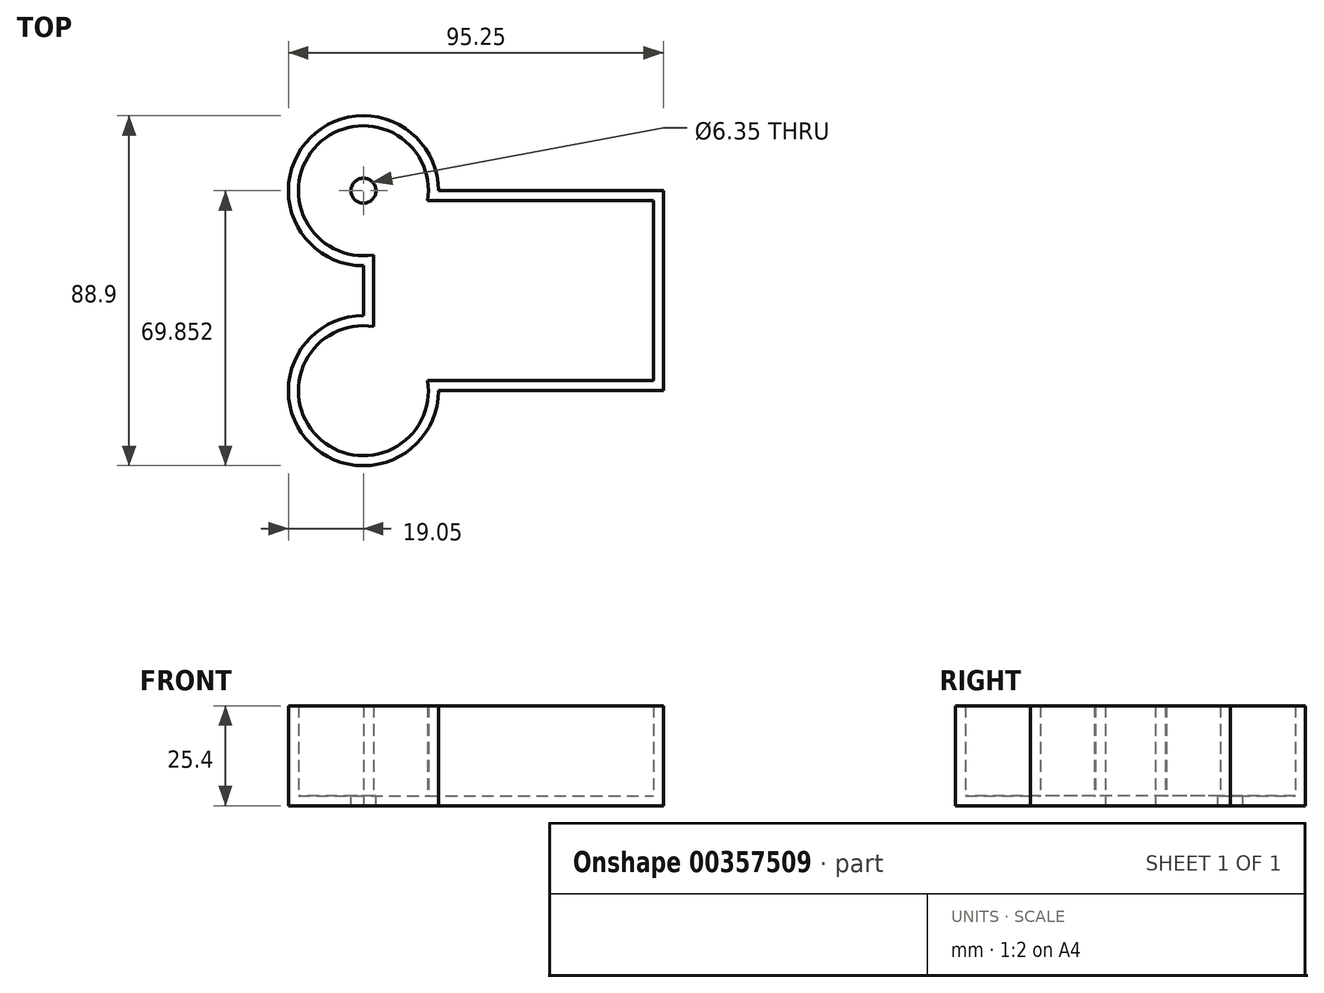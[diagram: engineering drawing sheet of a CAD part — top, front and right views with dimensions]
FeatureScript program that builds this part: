
annotation { "Feature Type Name" : "Feature", "Feature Type Description" : "" }
export const myFeature = defineFeature(function(context is Context, id is Id, definition is map)
    precondition{}
    {
        {
            var Q0;
            Q0=qCreatedBy(makeId("Top.planeOp"),FACE);
            var sketch = newSketch(context, id + "F0", { "sketchPlane" : qUnion([Q0])});
            skLineSegment(sketch, "E0.bottom", {"start": v(-34.16, 28.81) * mm, "end": v(42.04, 28.81) * mm});
            skLineSegment(sketch, "E0.top", {"start": v(-34.16, -21.99) * mm, "end": v(42.04, -21.99) * mm});
            skLineSegment(sketch, "E0.left", {"start": v(-34.16, 28.81) * mm, "end": v(-34.16, -21.99) * mm});
            skLineSegment(sketch, "E0.right", {"start": v(42.04, 28.81) * mm, "end": v(42.04, -21.99) * mm});
            skCircle(sketch, "E1", {"center": v(-34.16, 28.81) * mm, "radius": 19.05 * mm});
            skCircle(sketch, "E2", {"center": v(-34.16, -21.99) * mm, "radius": 19.05 * mm});
            skSolve(sketch);
        }
        {
            var Q0;
            {var subQ0=sQuery(id+"F0.wireOp",EDGE,"E0.right");Q0=makeQuery(id+"F0.imprint","IMPRINT",FACE,{"disambiguationData":[TD([[makeQuery(id+"F0.imprint","IMPRINT",EDGE,{"derivedFrom":subQ0}),-1.0]])]});}
            var Q1;
            {var subQ0=sQuery(id+"F0.wireOp",EDGE,"E0.left");var subQ1=sQuery(id+"F0.wireOp",EDGE,"E0.top");var subQ2=makeQuery(id+"F0.imprint","INTERSECT",VERTEX,{"derivedFrom":[subQ1,subQ0]});Q1=makeQuery(id+"F0.imprint","IMPRINT",FACE,{"disambiguationData":[TD([[makeQuery(id+"F0.imprint","IMPRINT",EDGE,{"disambiguationData":[TD([[subQ2,-1.0]])],"derivedFrom":subQ1}),1.0]])]});}
            var Q2;
            {var subQ0=sQuery(id+"F0.wireOp",EDGE,"E0.left");var subQ1=sQuery(id+"F0.wireOp",EDGE,"E0.top");var subQ2=makeQuery(id+"F0.imprint","INTERSECT",VERTEX,{"derivedFrom":[subQ1,subQ0]});Q2=makeQuery(id+"F0.imprint","IMPRINT",FACE,{"disambiguationData":[TD([[makeQuery(id+"F0.imprint","IMPRINT",EDGE,{"disambiguationData":[TD([[subQ2,-1.0]])],"derivedFrom":subQ1}),-1.0]])]});}
            var Q3;
            {var subQ0=sQuery(id+"F0.wireOp",EDGE,"E0.left");var subQ1=sQuery(id+"F0.wireOp",EDGE,"E0.bottom");var subQ2=makeQuery(id+"F0.imprint","INTERSECT",VERTEX,{"derivedFrom":[subQ1,subQ0]});Q3=makeQuery(id+"F0.imprint","IMPRINT",FACE,{"disambiguationData":[TD([[makeQuery(id+"F0.imprint","IMPRINT",EDGE,{"disambiguationData":[TD([[subQ2,-1.0]])],"derivedFrom":subQ1}),1.0]])]});}
            var Q4;
            {var subQ0=sQuery(id+"F0.wireOp",EDGE,"E0.left");var subQ1=sQuery(id+"F0.wireOp",EDGE,"E0.bottom");var subQ2=makeQuery(id+"F0.imprint","INTERSECT",VERTEX,{"derivedFrom":[subQ1,subQ0]});Q4=makeQuery(id+"F0.imprint","IMPRINT",FACE,{"disambiguationData":[TD([[makeQuery(id+"F0.imprint","IMPRINT",EDGE,{"disambiguationData":[TD([[subQ2,-1.0]])],"derivedFrom":subQ1}),-1.0]])]});}
            extrude(context, id + "F1", {"entities" : qUnion([Q0, Q1, Q2, Q3, Q4]), "depth" : 25.4 * mm});
        }
        {
            var Q0;
            Q0=makeQuery(id+"F1.opExtrude","CAP_FACE",FACE,{"disambiguationData":[OSD([sQuery(id+"F0.wireOp",EDGE,"E0.bottom"),sQuery(id+"F0.wireOp",EDGE,"E0.top"),sQuery(id+"F0.wireOp",EDGE,"E0.left"),sQuery(id+"F0.wireOp",EDGE,"E0.right"),sQuery(id+"F0.wireOp",EDGE,"E1"),sQuery(id+"F0.wireOp",EDGE,"E2")])],"isStart":false});
            shell(context, id + "F2", {"entities" : qUnion([Q0]), "thickness" : 2.54 * mm});
        }
        {
            var Q0;
            Q0=makeQuery(id+"F2.opShell","OFFSET_FACE",FACE,{"disambiguationData":[OSD([sQuery(id+"F0.wireOp",EDGE,"E0.bottom"),sQuery(id+"F0.wireOp",EDGE,"E0.top"),sQuery(id+"F0.wireOp",EDGE,"E0.left"),sQuery(id+"F0.wireOp",EDGE,"E0.right"),sQuery(id+"F0.wireOp",EDGE,"E1"),sQuery(id+"F0.wireOp",EDGE,"E2")])]});
            var sketch = newSketch(context, id + "F3", { "sketchPlane" : qUnion([Q0])});
            skCircle(sketch, "E3", {"center": v(-34.16, 28.81) * mm, "radius": 6.64 * mm});
            skCircle(sketch, "E4", {"center": v(-34.16, -21.99) * mm, "radius": 7.46 * mm});
            skSolve(sketch);
        }
        {
            var Q0;
            Q0=sQuery(id+"F3.wireOp",VERTEX,"E3.center");
            var Q1;
            Q1=makeQuery(id+"F1.opExtrude","SWEPT_BODY",BODY,{"disambiguationData":[OSD([sQuery(id+"F0.wireOp",EDGE,"E0.bottom"),sQuery(id+"F0.wireOp",EDGE,"E0.top"),sQuery(id+"F0.wireOp",EDGE,"E0.left"),sQuery(id+"F0.wireOp",EDGE,"E0.right"),sQuery(id+"F0.wireOp",EDGE,"E1"),sQuery(id+"F0.wireOp",EDGE,"E2")])]});
            hole(context, id + "F4", {"style" : HoleStyle.SIMPLE, "endStyle" : HoleEndStyle.THROUGH, "holeDiameter" : 6.35 * mm, "isTappedThrough" : true, "tappedDepth" : 12.7 * mm, "tapClearance" : 3, "locations" : qUnion([Q0]), "scope" : qUnion([Q1])});
        }
    });
